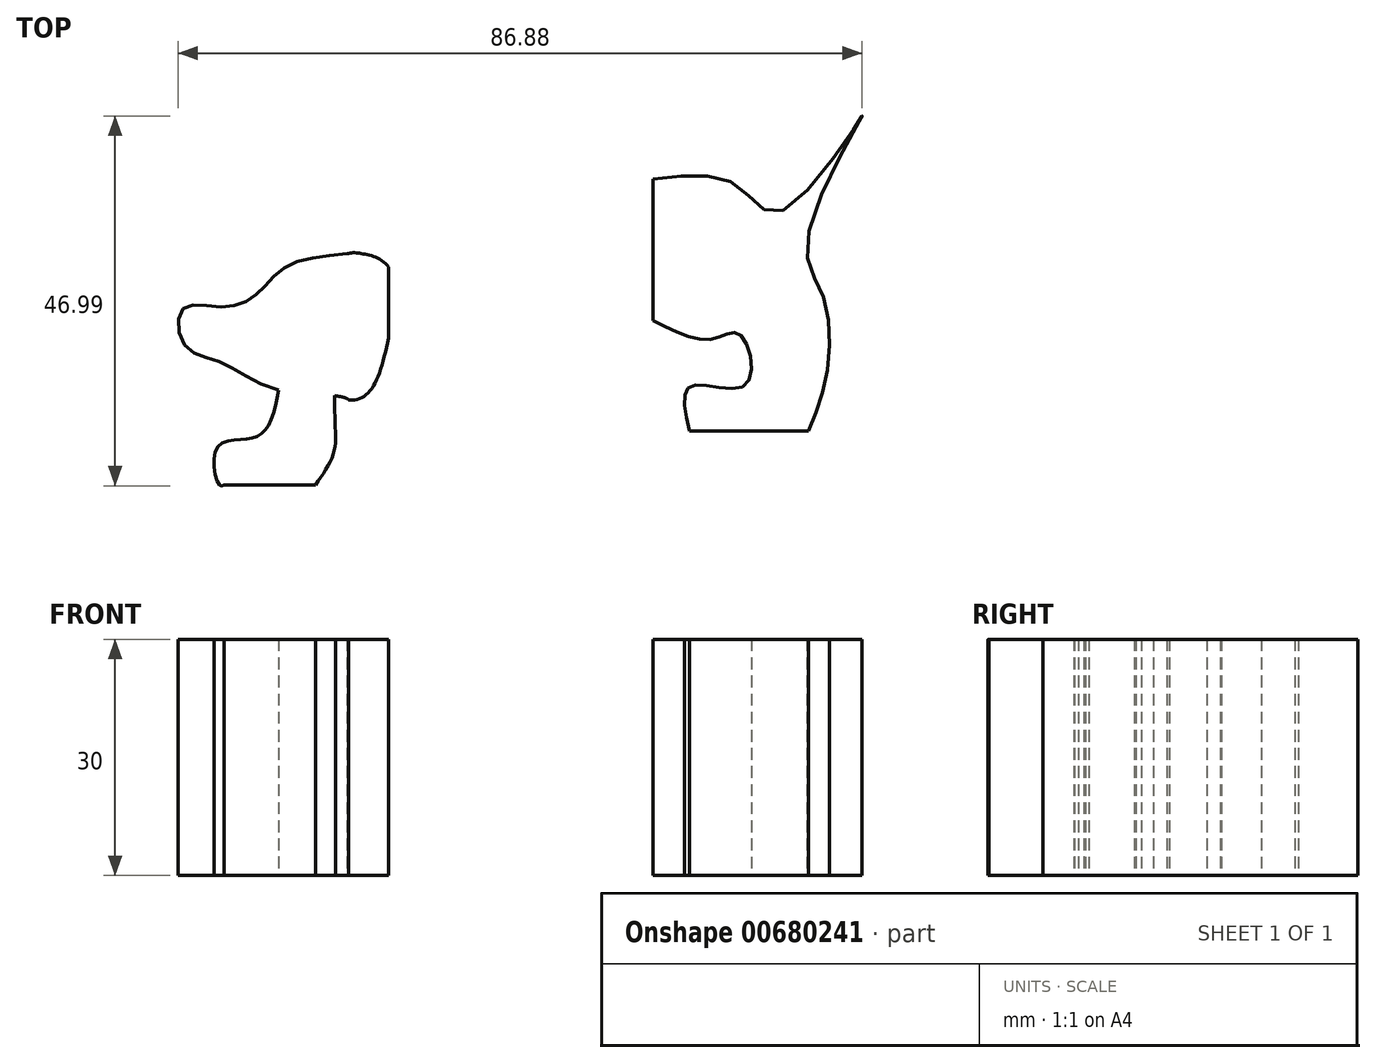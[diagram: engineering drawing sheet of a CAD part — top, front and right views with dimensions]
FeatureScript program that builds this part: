
annotation { "Feature Type Name" : "Feature", "Feature Type Description" : "" }
export const myFeature = defineFeature(function(context is Context, id is Id, definition is map)
    precondition{}
    {
        {
            var Q0;
            Q0=qCreatedBy(makeId("Top.planeOp"),FACE);
            var sketch = newSketch(context, id + "F0", { "sketchPlane" : qUnion([Q0])});
            skLineSegment(sketch, "E0.bottom", {"start": v(-44.57, 38.75) * mm, "end": v(-14.57, 38.75) * mm, "construction": true});
            skLineSegment(sketch, "E0.top", {"start": v(-44.57, -1.25) * mm, "end": v(-14.57, -1.25) * mm, "construction": true});
            skLineSegment(sketch, "E0.left", {"start": v(-44.57, 38.75) * mm, "end": v(-44.57, -1.25) * mm, "construction": true});
            skLineSegment(sketch, "E0.right", {"start": v(-14.57, 38.75) * mm, "end": v(-14.57, -1.25) * mm, "construction": true});
            skLineSegment(sketch, "E1", {"start": v(-16.33, 30.75) * mm, "end": v(-16.33, 12.75) * mm});
            skFitSpline(sketch, "E2", {"points": [v(-16.33, 30.75) * mm, v(-19.62, 32.47) * mm, v(-21.55, 32.47) * mm, v(-23.67, 30.75) * mm, v(-24.83, 26.28) * mm, v(-26, 21.06) * mm, v(-25.6, 16.43) * mm, v(-21.35, 13.91) * mm, v(-18.65, 15.07) * mm, v(-16.33, 21.75) * mm, v(-16.33, 30.75) * mm]});
            skFitSpline(sketch, "E3", {"points": [v(-21.55, 32.47) * mm, v(-29.47, 30.75) * mm, v(-33.14, 27.25) * mm, v(-37.59, 25.7) * mm, v(-42.42, 25.5) * mm, v(-42.23, 20.87) * mm, v(-37.78, 18.75) * mm, v(-30.24, 15.16) * mm, v(-21.35, 13.91) * mm, v(-21.35, 12.37) * mm], "startDerivative": vector(-65.98, -5.8) * mm, "endDerivative": vector(-10.4, -30.04) * mm});
            skLineSegment(sketch, "E4", {"start": v(-40.1, 15.16) * mm, "end": v(-40.1, 3.1) * mm});
            skFitSpline(sketch, "E5", {"points": [v(-30.24, 15.16) * mm, v(-31.98, 10.05) * mm, v(-34.69, 8.89) * mm, v(-38.17, 7.73) * mm, v(-37.78, 3.1) * mm, v(-37.2, 3.1) * mm], "startDerivative": vector(-4.89, -23.17) * mm, "endDerivative": vector(6.77, 3.32) * mm});
            skLineSegment(sketch, "E6", {"start": v(-37.2, 3.1) * mm, "end": v(-25.6, 3.1) * mm});
            skFitSpline(sketch, "E7", {"points": [v(-25.6, 3.1) * mm, v(-23.29, 7.15) * mm, v(-23.1, 10.63) * mm, v(-23.16, 14.43) * mm], "startDerivative": vector(8, 11.28) * mm, "endDerivative": vector(-0.06, 11.8) * mm});
            skSolve(sketch);
        }
        {
            var Q0;
            Q0=qCreatedBy(makeId("Top.planeOp"),FACE);
            var sketch = newSketch(context, id + "F1", { "sketchPlane" : qUnion([Q0])});
            skLineSegment(sketch, "E8.bottom", {"start": v(13.84, 9.95) * mm, "end": v(43.84, 9.95) * mm, "construction": true});
            skLineSegment(sketch, "E8.top", {"start": v(13.84, 49.95) * mm, "end": v(43.84, 49.95) * mm, "construction": true});
            skLineSegment(sketch, "E8.left", {"start": v(13.84, 9.95) * mm, "end": v(13.84, 49.95) * mm, "construction": true});
            skLineSegment(sketch, "E8.right", {"start": v(43.84, 9.95) * mm, "end": v(43.84, 49.95) * mm, "construction": true});
            skLineSegment(sketch, "E9", {"start": v(17.3, 41.96) * mm, "end": v(17.3, 23.96) * mm});
            skFitSpline(sketch, "E10", {"points": [v(17.3, 23.96) * mm, v(24.83, 21.64) * mm, v(28.31, 22.22) * mm, v(29.08, 15.85) * mm, v(22.13, 15.65) * mm, v(21.93, 9.95) * mm], "startDerivative": vector(35.54, -17.69) * mm, "endDerivative": vector(9.2, -39.38) * mm});
            skLineSegment(sketch, "E11", {"start": v(21.93, 9.95) * mm, "end": v(37, 9.95) * mm});
            skFitSpline(sketch, "E12", {"points": [v(37, 9.95) * mm, v(39.33, 17) * mm, v(38.94, 26.86) * mm, v(37, 34.98) * mm, v(43.84, 49.95) * mm, v(33.53, 37.88) * mm, v(27.92, 41.16) * mm, v(17.3, 41.96) * mm], "startDerivative": vector(22.65, 53.8) * mm, "endDerivative": vector(-83.1, -10.19) * mm});
            skLineSegment(sketch, "E13", {"start": v(51.5, 22.22) * mm, "end": v(51.5, 9.95) * mm});
            skSolve(sketch);
        }
        {
            var Q0;
            Q0=makeQuery(id+"F1.imprint","IMPRINT",FACE,{"disambiguationData":[TD([[makeQuery(id+"F1.imprint","IMPRINT",EDGE,{"derivedFrom":sQuery(id+"F1.wireOp",EDGE,"E9")}),1.0]])]});
            extrude(context, id + "F2", {"entities" : qUnion([Q0]), "depth" : 30 * mm, "offsetDistance" : 25 * mm});
        }
        {
            var Q0;
            {var subQ0=sQuery(id+"F0.wireOp",EDGE,"E3");var subQ1=sQuery(id+"F0.wireOp",EDGE,"E2");var subQ2=makeQuery(id+"F0.imprint","INTERSECT",VERTEX,{"disambiguationData":[OD(0.0)],"derivedFrom":[subQ1,subQ0]});Q0=makeQuery(id+"F0.imprint","IMPRINT",FACE,{"disambiguationData":[TD([[makeQuery(id+"F0.imprint","IMPRINT",EDGE,{"disambiguationData":[TD([[subQ2,-1.0]])],"derivedFrom":subQ0}),1.0]])]});}
            var Q1;
            {var subQ0=sQuery(id+"F0.wireOp",EDGE,"E2");var subQ1=sQuery(id+"F0.wireOp",EDGE,"E1");var subQ7=makeQuery(id+"F0.imprint","INTERSECT",VERTEX,{"disambiguationData":[OD(0.0)],"derivedFrom":[subQ1,subQ0]});Q1=makeQuery(id+"F0.imprint","IMPRINT",FACE,{"disambiguationData":[TD([[makeQuery(id+"F0.imprint","IMPRINT",EDGE,{"disambiguationData":[TD([[subQ7,-1.0]])],"derivedFrom":subQ1}),-1.0]])]});}
            var Q2;
            {var subQ0=sQuery(id+"F0.wireOp",EDGE,"E5");Q2=makeQuery(id+"F0.imprint","IMPRINT",FACE,{"disambiguationData":[TD([[makeQuery(id+"F0.imprint","IMPRINT",EDGE,{"derivedFrom":subQ0}),1.0]])]});}
            extrude(context, id + "F3", {"entities" : qUnion([Q0, Q1, Q2]), "depth" : 30 * mm, "offsetDistance" : 25 * mm});
        }
    });
